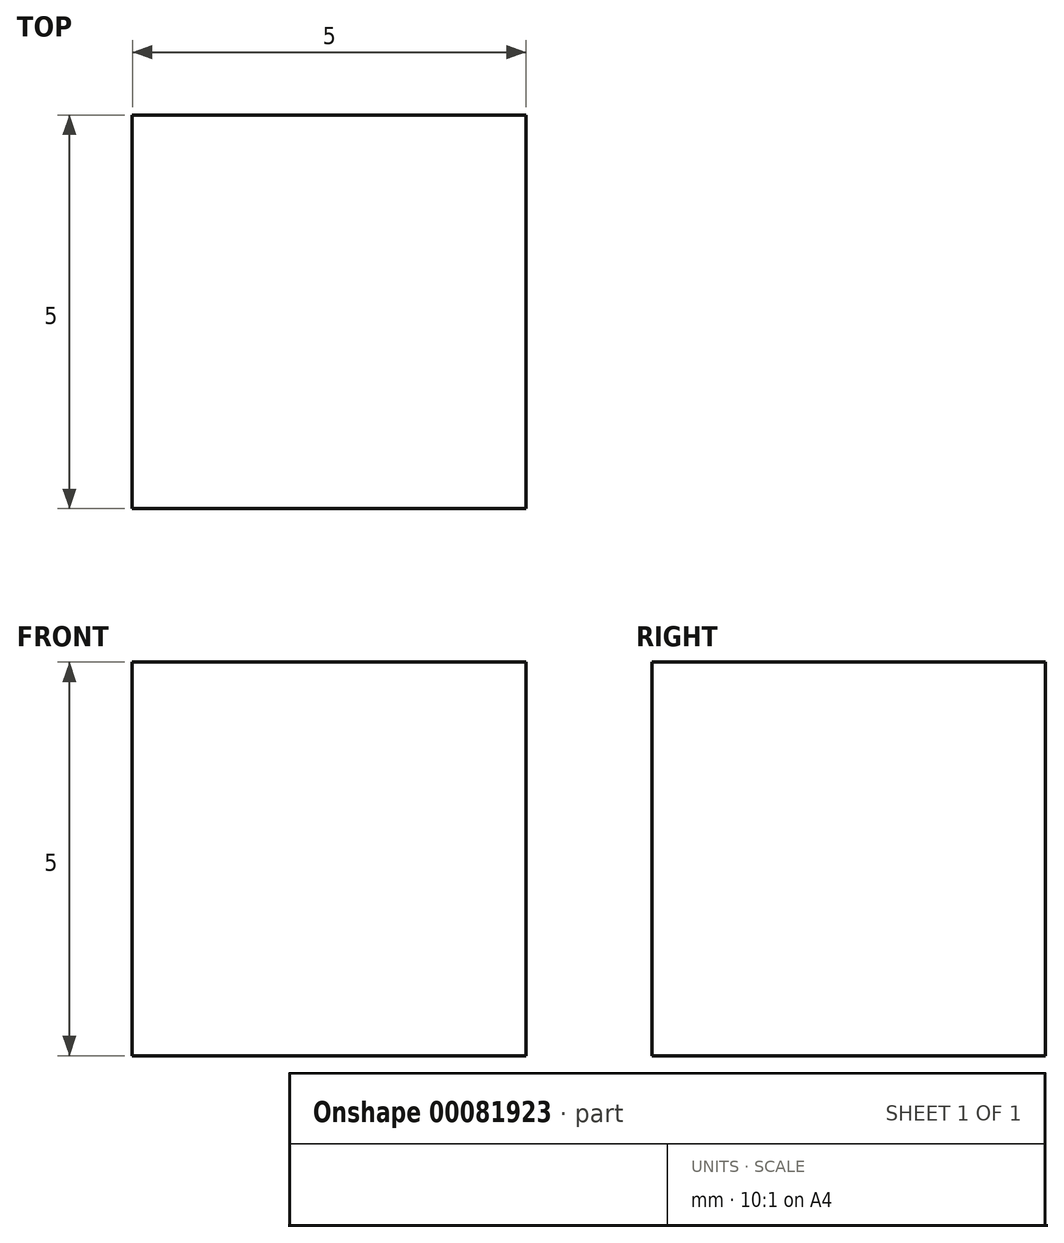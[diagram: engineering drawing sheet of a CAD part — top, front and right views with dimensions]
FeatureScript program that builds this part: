
annotation { "Feature Type Name" : "Feature", "Feature Type Description" : "" }
export const myFeature = defineFeature(function(context is Context, id is Id, definition is map)
    precondition{}
    {
        {
            var Q0;
            Q0=qCreatedBy(makeId("Top.planeOp"),FACE);
            var sketch = newSketch(context, id + "F0", { "sketchPlane" : qUnion([Q0])});
            skLineSegment(sketch, "E0.bottom", {"start": v(-45.46, -40.46) * mm, "end": v(-40.46, -40.46) * mm});
            skLineSegment(sketch, "E0.top", {"start": v(-45.46, -45.46) * mm, "end": v(-40.46, -45.46) * mm});
            skLineSegment(sketch, "E0.left", {"start": v(-45.46, -40.46) * mm, "end": v(-45.46, -45.46) * mm});
            skLineSegment(sketch, "E0.right", {"start": v(-40.46, -40.46) * mm, "end": v(-40.46, -45.46) * mm});
            skSolve(sketch);
        }
        {
            var Q0;
            Q0 = qSketchRegion(id + "F0", true);
            extrude(context, id + "F1", {"entities" : qUnion([Q0]), "depth" : 5 * mm});
        }
    });
